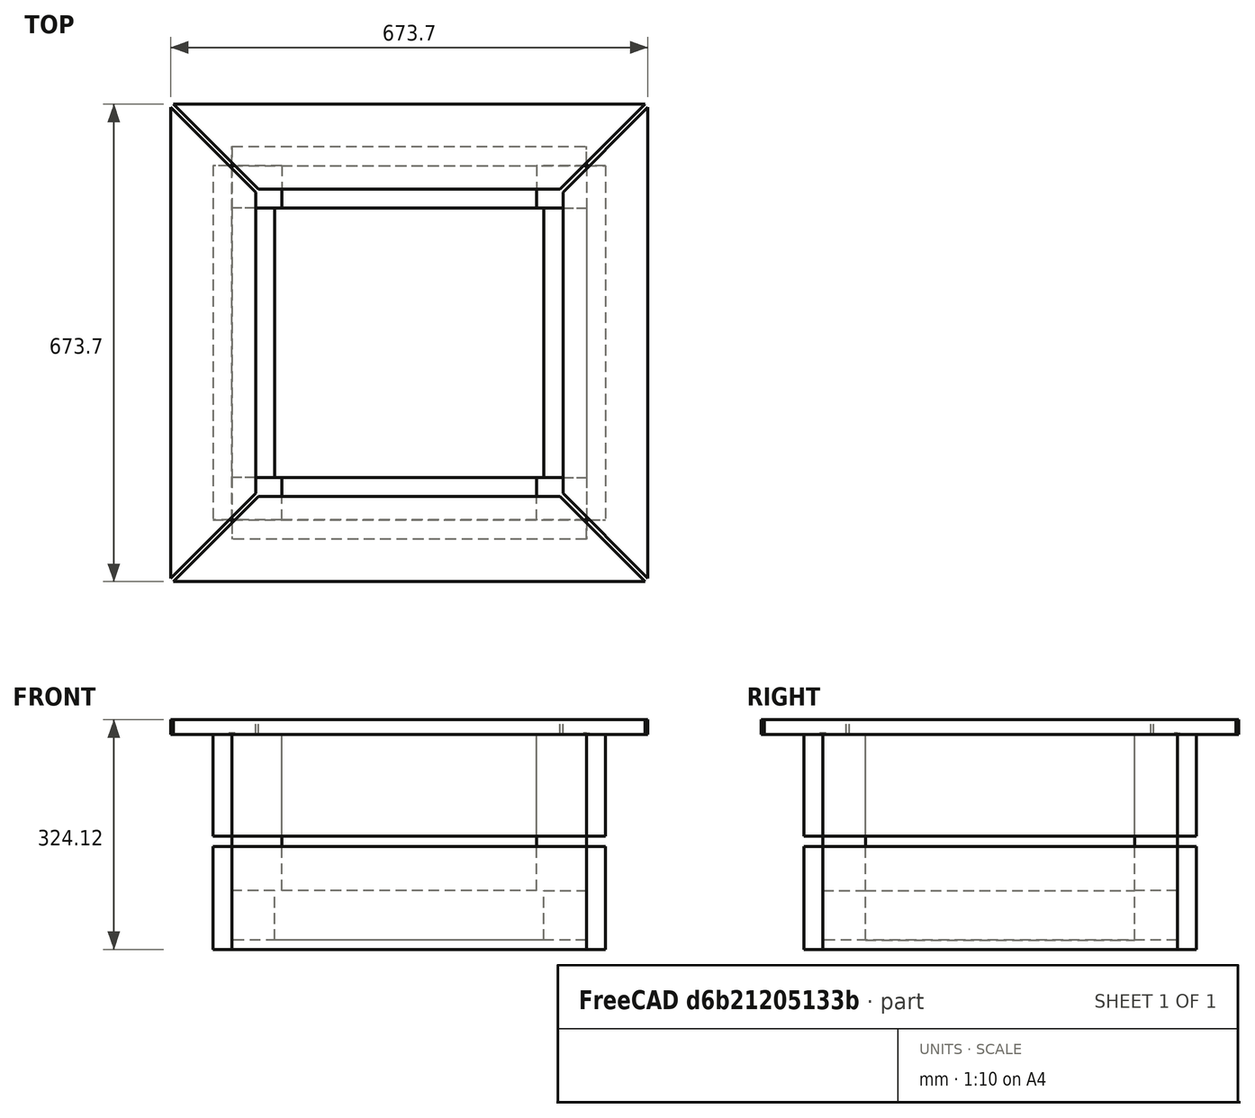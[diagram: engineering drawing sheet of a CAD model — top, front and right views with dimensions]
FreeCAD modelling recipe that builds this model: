
FCSTD DOCUMENT  (FreeCAD 0.18R16131 (Git))
Label: jardiniereBasse
License: All rights reserved
LicenseURL: http://en.wikipedia.org/wiki/All_rights_reserved
objects: TechDraw::DrawViewPart×6, TechDraw::DrawViewDimension×6, Sketcher::SketchObject×4, PartDesign::Pad×4, PartDesign::Mirrored×4, TechDraw::DrawViewAnnotation×4, PartDesign::Plane×3, PartDesign::MultiTransform×3, PartDesign::PolarPattern×2, TechDraw::DrawViewSection×2, PartDesign::LinearPattern×1, PartDesign::Body×1, TechDraw::DrawSVGTemplate×1, TechDraw::DrawPage×1
note: 26 computed .brp shape members not serialized (recipe doc carries the construction recipe); baked Part::Feature solids carry a one-line shape summary decoded from their .brp

FEATURE [Sketcher::SketchObject] Sketch
  MapMode = 5
  Support = -> [XY_Plane]
  sketch-geometry (8):
    g0: LineSegment StartX=-250 StartY=250 StartZ=0 EndX=250 EndY=250 EndZ=0
    g1: LineSegment StartX=250 StartY=250 StartZ=0 EndX=250 EndY=-250 EndZ=0
    g2: LineSegment StartX=250 StartY=-250 StartZ=0 EndX=-250 EndY=-250 EndZ=0
    g3: LineSegment StartX=-250 StartY=-250 StartZ=0 EndX=-250 EndY=250 EndZ=0
    g4: LineSegment StartX=-190 StartY=190 StartZ=0 EndX=190 EndY=190 EndZ=0
    g5: LineSegment StartX=190 StartY=190 StartZ=0 EndX=190 EndY=-190 EndZ=0
    g6: LineSegment StartX=190 StartY=-190 StartZ=0 EndX=-190 EndY=-190 EndZ=0
    g7: LineSegment StartX=-190 StartY=-190 StartZ=0 EndX=-190 EndY=190 EndZ=0
  constraints (22):
    c: Coincident(g0,g1)
    c: Vertical(g1)
    c: Coincident(g1,g2)
    c: Horizontal(g2)
    c: Coincident(g2,g3)
    c: Coincident(g3,g0)
    c: DistanceX(g0,g0) = 500
    c: DistanceY(g3,g3) = 500
    c: Symmetric(g0,g2,g-1)
    c: Symmetric(g0,g0,g-2)
    c: Coincident(g4,g5)
    c: Coincident(g5,g6)
    c: Coincident(g6,g7)
    c: Coincident(g7,g4)
    c: Horizontal(g4)
    c: Horizontal(g6)
    c: Vertical(g5)
    c: Vertical(g7)
    c: DistanceX(g5,g1) = 60
    c: DistanceY(g1,g5) = 60
    c: DistanceY(g4,g0) = 60
    c: DistanceX(g0,g4) = 60
FEATURE [PartDesign::Pad] Pad
  Length = 70
  Length2 = 100
  Profile = -> Sketch
  Type = 0
FEATURE [PartDesign::Plane] DatumPlane
  Length = 600
  MapMode = 5
  Placement = pos=(0,0,70) rot=(0,0,1;0rad)
  ResizeMode = 0
  Support = -> [Pad]
  Width = 600
FEATURE [Sketcher::SketchObject] Sketch001
  ExternalGeometry = -> [Pad]
  MapMode = 5
  Placement = pos=(0,0,70) rot=(0,0,1;0rad)
  Support = -> [DatumPlane]
  sketch-geometry (4):
    g0: LineSegment StartX=-250 StartY=250 StartZ=0 EndX=-180 EndY=250 EndZ=0
    g1: LineSegment StartX=-180 StartY=250 StartZ=0 EndX=-180 EndY=190 EndZ=0
    g2: LineSegment StartX=-180 StartY=190 StartZ=0 EndX=-250 EndY=190 EndZ=0
    g3: LineSegment StartX=-250 StartY=190 StartZ=0 EndX=-250 EndY=250 EndZ=0
  constraints (11):
    c: Coincident(g0,g1)
    c: Coincident(g1,g2)
    c: Coincident(g2,g3)
    c: Coincident(g3,g0)
    c: Horizontal(g0)
    c: Horizontal(g2)
    c: Vertical(g1)
    c: Vertical(g3)
    c: Coincident(g0,g-4)
    c: DistanceX(g0,g0) = 70
    c: DistanceY(g3,g3) = 60
FEATURE [PartDesign::Pad] Pad001
  BaseFeature = -> Pad
  Length = 220
  Length2 = 100
  Profile = -> Sketch001
  Type = 0
FEATURE [PartDesign::Mirrored] Mirrored
  MirrorPlane = -> Sketch001 [H_Axis]
FEATURE [PartDesign::Mirrored] Mirrored001
  MirrorPlane = -> Sketch001 [V_Axis]
FEATURE [PartDesign::MultiTransform] MultiTransform
  BaseFeature = -> Pad001
  Originals = -> [Pad001]
  Transformations = -> [Mirrored,Mirrored001]
FEATURE [PartDesign::Plane] DatumPlane001
  Length = 577.46
  MapMode = 5
  Placement = pos=(0,250,0) rot=(0,0.707107,0.707107;3.14159rad)
  ResizeMode = 0
  Support = -> [Pad001]
  Width = 377.46
FEATURE [Sketcher::SketchObject] Sketch002
  ExternalGeometry = -> [MultiTransform]
  MapMode = 5
  Placement = pos=(0,250,0) rot=(0,0.707107,0.707107;3.14159rad)
  Support = -> [DatumPlane001]
  sketch-geometry (4):
    g0: LineSegment StartX=-250 StartY=131.878 StartZ=0 EndX=250 EndY=131.878 EndZ=0
    g1: LineSegment StartX=250 StartY=131.878 StartZ=0 EndX=250 EndY=-13.1218 EndZ=0
    g2: LineSegment StartX=250 StartY=-13.1218 StartZ=0 EndX=-250 EndY=-13.1218 EndZ=0
    g3: LineSegment StartX=-250 StartY=-13.1218 StartZ=0 EndX=-250 EndY=131.878 EndZ=0
  constraints (11):
    c: Coincident(g0,g1)
    c: Coincident(g1,g2)
    c: Coincident(g2,g3)
    c: Coincident(g3,g0)
    c: Horizontal(g0)
    c: Horizontal(g2)
    c: Vertical(g1)
    c: Vertical(g3)
    c: PointOnObject(g1,g-4)
    c: DistanceY(g3,g3) = 145
    c: PointOnObject(g0,g-3)
FEATURE [PartDesign::Pad] Pad002
  BaseFeature = -> MultiTransform
  Length = 27
  Length2 = 100
  Profile = -> Sketch002
  Type = 0
FEATURE [PartDesign::LinearPattern] LinearPattern
  Direction = -> Sketch002 [V_Axis]
  Length = 160
  Occurrences = 2
FEATURE [PartDesign::Mirrored] Mirrored002
  MirrorPlane = -> XZ_Plane
FEATURE [PartDesign::PolarPattern] PolarPattern
  Angle = 90
  Axis = -> Z_Axis
  Occurrences = 2
FEATURE [PartDesign::MultiTransform] MultiTransform001
  BaseFeature = -> Pad002
  Originals = -> [Pad002]
  Transformations = -> [LinearPattern,Mirrored002,PolarPattern]
FEATURE [PartDesign::Plane] DatumPlane002
  Length = 600
  MapMode = 5
  Placement = pos=(0,0,290) rot=(0,0,1;0rad)
  ResizeMode = 0
  Support = -> [MultiTransform001]
  Width = 600
FEATURE [Sketcher::SketchObject] Sketch003
  MapMode = 5
  Placement = pos=(0,0,290) rot=(0,0,1;0rad)
  Support = -> [DatumPlane002]
  sketch-geometry (4):
    g0: LineSegment StartX=-332.5 StartY=336.85 StartZ=0 EndX=332.5 EndY=336.85 EndZ=0
    g1: LineSegment StartX=332.5 StartY=336.85 StartZ=0 EndX=212.5 EndY=216.85 EndZ=0
    g2: LineSegment StartX=212.5 StartY=216.85 StartZ=0 EndX=-212.5 EndY=216.85 EndZ=0
    g3: LineSegment StartX=-212.5 StartY=216.85 StartZ=0 EndX=-332.5 EndY=336.85 EndZ=0
  constraints (10):
    c: Coincident(g0,g1)
    c: Coincident(g1,g2)
    c: Coincident(g2,g3)
    c: Coincident(g3,g0)
    c: Angle(g3,g0) = 0.785398
    c: Angle(g0,g1) = 0.785398
    c: DistanceX(g2,g2) = 425
    c: DistanceY(g1,g0) = 120
    c: DistanceX(g0,g0) = 665
    c: Symmetric(g2,g1,g-2)
FEATURE [PartDesign::Pad] Pad003
  BaseFeature = -> MultiTransform001
  Length = 21
  Length2 = 100
  Profile = -> Sketch003
  Type = 0
FEATURE [PartDesign::Mirrored] Mirrored003
  MirrorPlane = -> Sketch003 [H_Axis]
FEATURE [PartDesign::PolarPattern] PolarPattern001
  Angle = 90
  Axis = -> Sketch003 [N_Axis]
  Occurrences = 2
FEATURE [PartDesign::MultiTransform] MultiTransform002
  BaseFeature = -> Pad003
  Originals = -> [Pad003]
  Transformations = -> [Mirrored003,PolarPattern001]
FEATURE [PartDesign::Body] Body
  Group = -> [Sketch,Pad,DatumPlane,Sketch001,Pad001,MultiTransform,Mirrored,Mirrored001,DatumPlane001,Sketch002,Pad002,MultiTransform001,LinearPattern,Mirrored002,PolarPattern,DatumPlane002,Sketch003,Pad003,MultiTransform002,Mirrored003,PolarPattern001]
  Origin = -> Origin
  Tip = -> MultiTransform002
FEATURE [TechDraw::DrawSVGTemplate] Template
  EditableTexts = Designed_by_Name=Y. Labrit; Drawing_number=Drawing number; FC-Date=01/07/2018; FC-SC=Scale; FC-SH=Sheet; FC-Title=Jardiniere cube; Subtitle=Subtitle; Weight=Weight
  Height = 210
  Orientation = 1
  Width = 297
FEATURE [TechDraw::DrawViewPart] View
  CoarseView = false
  Direction = (0,1,0)
  Focus = 100
  HardHidden = false
  IsoCount = 0
  IsoHidden = false
  IsoVisible = false
  LockPosition = false
  Perspective = false
  Rotation = 0
  Scale = 0.07
  ScaleType = 2
  SeamHidden = false
  SeamVisible = false
  SmoothHidden = false
  SmoothVisible = false
  Source = -> [MultiTransform002]
  X = 58.3303
  Y = 105.073
FEATURE [TechDraw::DrawViewSection] Section  label="Section A - A"
  BaseView = -> View
  CoarseView = false
  Direction = (0,0,1)
  Focus = 100
  FuseBeforeCut = true
  HardHidden = false
  HatchScale = 1
  IsoCount = 0
  IsoHidden = false
  IsoVisible = false
  LockPosition = false
  NameGeomPattern = Diamond
  Perspective = false
  Rotation = 0
  Scale = 0.07
  ScaleType = 2
  SeamHidden = false
  SeamVisible = false
  SectionDirection = 3
  SectionNormal = (0,0,1)
  SectionOrigin = (2.84e-14,2.84e-14,136.045)
  SectionSymbol = A
  SmoothHidden = false
  SmoothVisible = false
  Source = -> [MultiTransform002]
  X = 57.2775
  Y = 45.8237
FEATURE [TechDraw::DrawViewSection] Section001  label="Section A - A001"
  BaseView = -> View
  CoarseView = false
  Direction = (1,0,0)
  Focus = 100
  FuseBeforeCut = true
  HardHidden = false
  HatchScale = 1
  IsoCount = 0
  IsoHidden = false
  IsoVisible = false
  LockPosition = false
  NameGeomPattern = Diamond
  Perspective = false
  Rotation = 0
  Scale = 0.07
  ScaleType = 2
  SeamHidden = false
  SeamVisible = false
  SectionDirection = 0
  SectionNormal = (1,0,0)
  SectionOrigin = (2.84e-14,2.84e-14,136.045)
  SectionSymbol = A
  SmoothHidden = false
  SmoothVisible = false
  Source = -> [MultiTransform002]
  X = 118.765
  Y = 105.919
FEATURE [TechDraw::DrawViewPart] View001
  CoarseView = true
  Direction = (0,0,1)
  Focus = 100
  HardHidden = false
  IsoCount = 0
  IsoHidden = false
  IsoVisible = false
  LockPosition = false
  Perspective = false
  Rotation = 0
  Scale = 0.05
  ScaleType = 2
  SeamHidden = false
  SeamVisible = false
  SmoothHidden = false
  SmoothVisible = false
  Source = -> [MultiTransform002]
  X = 57.2911
  Y = 163.823
FEATURE [TechDraw::DrawViewDimension] Dimension017
  Arbitrary = false
  FormatSpec = %.2f
  LockPosition = false
  MeasureType = 1
  OverTolerance = 0
  References2D = -> [Section001]
  Rotation = 0
  ScaleType = 0
  Type = 1
  UnderTolerance = 0
  X = 35.1592
  Y = -28.482
FEATURE [TechDraw::DrawViewAnnotation] Annotation
  Font = Times New Roman
  LineSpace = 80
  LockPosition = false
  MaxWidth = -1
  Rotation = 0
  ScaleType = 0
  Text = Base: 50x7x5 (2) / 40x7x5 (2) | Montants: 52x7x5 (4) | Cotes: 50x14,5x2,7 (16) | Cache: 66,5x12x2,1 (4)
  TextSize = 4
  TextStyle = 0
  X = 245.002
  Y = 105.167
FEATURE [TechDraw::DrawViewAnnotation] Annotation001
  Font = Times New Roman
  LineSpace = 80
  LockPosition = false
  MaxWidth = -1
  Rotation = 0
  ScaleType = 0
  Text = Base: 5x130mn (4) | Montants: 5x30 mn (4) | Cotes: 5x50 mn (72) | Cache: 5x50mn (8)
  TextSize = 4
  TextStyle = 0
  X = 235.051
  Y = 71.1326
FEATURE [TechDraw::DrawViewAnnotation] Annotation002
  Font = osifont
  LineSpace = 80
  LockPosition = false
  MaxWidth = -1
  Rotation = 0
  ScaleType = 0
  Text = Bois
  TextSize = 8
  TextStyle = 0
  X = 190.57
  Y = 120.647
FEATURE [TechDraw::DrawViewAnnotation] Annotation003
  Font = osifont
  LineSpace = 80
  LockPosition = false
  MaxWidth = -1
  Rotation = 0
  ScaleType = 0
  Text = Vis
  TextSize = 8
  TextStyle = 0
  X = 187.238
  Y = 87.8691
FEATURE [TechDraw::DrawViewPart] View004
  CoarseView = false
  Direction = (0.727,0.308,0.614)
  Focus = 100
  HardHidden = false
  IsoCount = 0
  IsoHidden = false
  IsoVisible = false
  LockPosition = false
  Perspective = false
  Rotation = 0
  Scale = 0.05
  ScaleType = 2
  SeamHidden = false
  SeamVisible = false
  SmoothHidden = false
  SmoothVisible = false
  Source = -> [MultiTransform002]
  X = 262.302
  Y = 170.37
FEATURE [TechDraw::DrawViewPart] View005
  CoarseView = false
  Direction = (0.727,0.308,0.614)
  Focus = 100
  HardHidden = false
  IsoCount = 0
  IsoHidden = false
  IsoVisible = false
  LockPosition = false
  Perspective = false
  Rotation = 0
  Scale = 0.05
  ScaleType = 2
  SeamHidden = false
  SeamVisible = false
  SmoothHidden = false
  SmoothVisible = false
  Source = -> [Pad002]
  X = 179.303
  Y = 167.734
FEATURE [TechDraw::DrawViewPart] View006
  CoarseView = false
  Direction = (0.727,0.308,0.614)
  Focus = 100
  HardHidden = false
  IsoCount = 0
  IsoHidden = false
  IsoVisible = false
  LockPosition = false
  Perspective = false
  Rotation = 0
  Scale = 0.05
  ScaleType = 2
  SeamHidden = false
  SeamVisible = false
  SmoothHidden = false
  SmoothVisible = false
  Source = -> [Pad003,MultiTransform001]
  X = 219.681
  Y = 169.095
FEATURE [TechDraw::DrawViewPart] View007
  CoarseView = false
  Direction = (0.727,0.308,0.614)
  Focus = 100
  HardHidden = false
  IsoCount = 0
  IsoHidden = false
  IsoVisible = false
  LockPosition = false
  Perspective = false
  Rotation = 0
  Scale = 0.05
  ScaleType = 2
  SeamHidden = false
  SeamVisible = false
  SmoothHidden = false
  SmoothVisible = false
  Source = -> [Pad]
  X = 139.066
  Y = 164.409
FEATURE [TechDraw::DrawViewDimension] Dimension032
  Arbitrary = false
  FormatSpec = %.2f
  LockPosition = false
  MeasureType = 1
  OverTolerance = 0
  References2D = -> [Section]
  Rotation = 0
  ScaleType = 0
  Type = 2
  UnderTolerance = 0
  X = 29.7358
  Y = -2.06917
FEATURE [TechDraw::DrawViewDimension] Dimension
  Arbitrary = false
  FormatSpec = %.2f
  LockPosition = false
  MeasureType = 1
  OverTolerance = 0
  References2D = -> [Section]
  Rotation = 0
  ScaleType = 0
  Type = 1
  UnderTolerance = 0
  X = -2.23026
  Y = 29.6552
FEATURE [TechDraw::DrawViewDimension] Dimension035
  Arbitrary = false
  FormatSpec = %.2f
  LockPosition = false
  MeasureType = 1
  OverTolerance = 0
  References2D = -> [View001]
  Rotation = 0
  ScaleType = 0
  Type = 2
  UnderTolerance = 0
  X = 22.8168
  Y = 0.153517
FEATURE [TechDraw::DrawViewDimension] Dimension036
  Arbitrary = false
  FormatSpec = %.2f
  LockPosition = false
  MeasureType = 1
  OverTolerance = 0
  References2D = -> [Section001]
  Rotation = 0
  ScaleType = 0
  Type = 2
  UnderTolerance = 0
  X = 33.735
  Y = 8.5776
FEATURE [TechDraw::DrawViewDimension] Dimension037
  Arbitrary = false
  FormatSpec = %.2f
  LockPosition = false
  MeasureType = 1
  OverTolerance = 0
  References2D = -> [Section001]
  Rotation = 0
  ScaleType = 0
  Type = 2
  UnderTolerance = 0
  X = -29.7558
  Y = 25.8901
FEATURE [TechDraw::DrawPage] Page
  KeepUpdated = true
  ProjectionType = 0
  Template = -> Template
  Views = -> [View,Section,Section001,View001,Dimension017,Annotation,Annotation001,Annotation002,Annotation003,View004,View005,View006,View007,Dimension032,Dimension,Dimension035,Dimension036,Dimension037]
